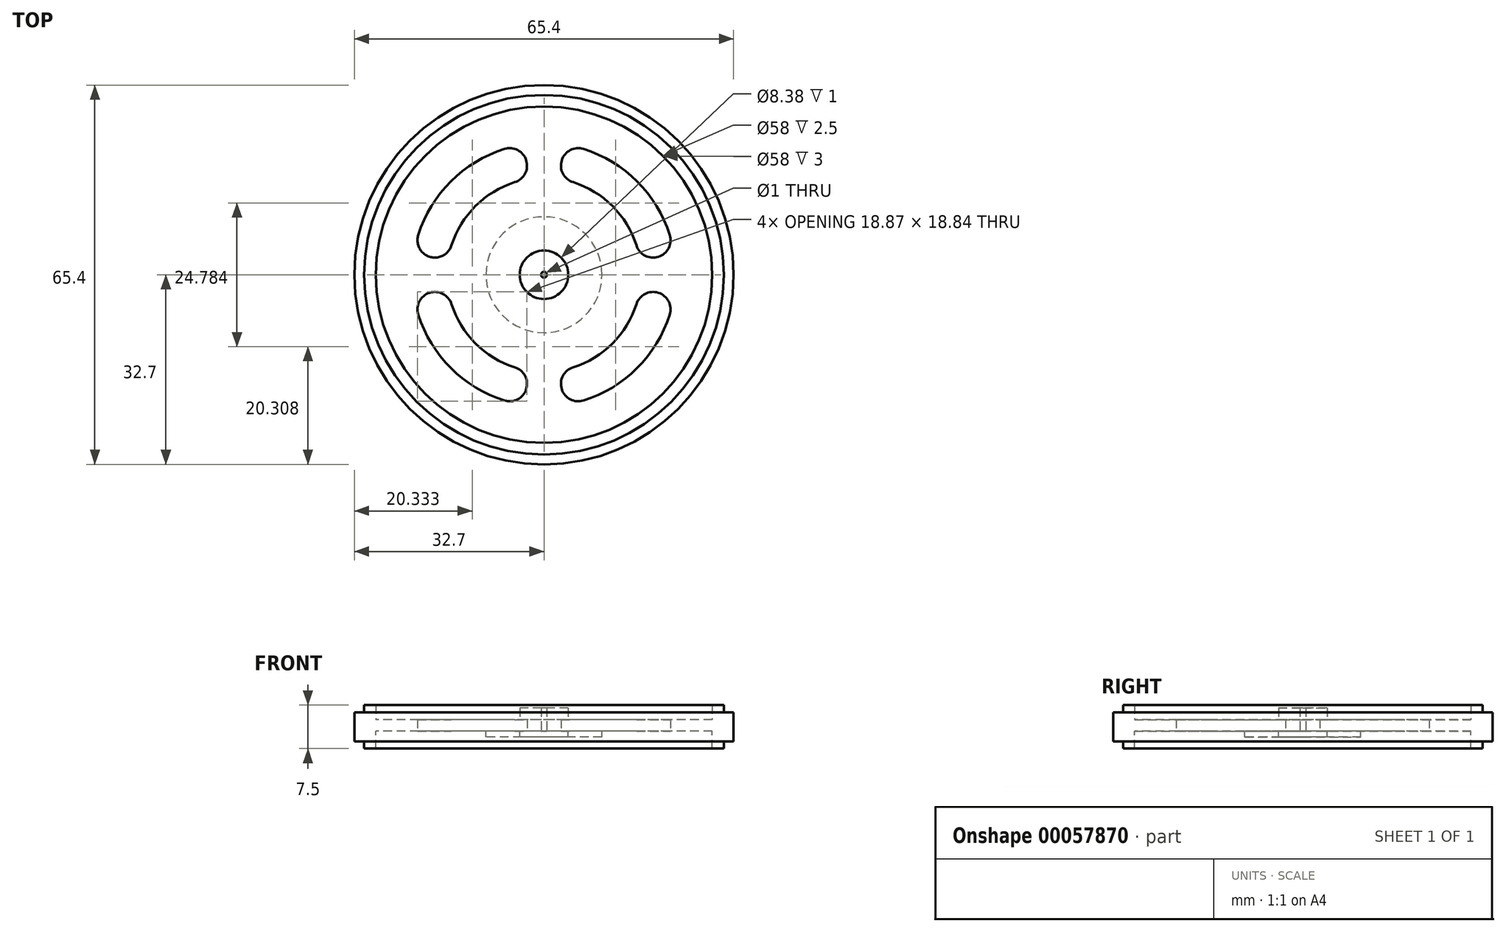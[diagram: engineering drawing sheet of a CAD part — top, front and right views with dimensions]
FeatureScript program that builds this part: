
annotation { "Feature Type Name" : "Feature", "Feature Type Description" : "" }
export const myFeature = defineFeature(function(context is Context, id is Id, definition is map)
    precondition{}
    {
        {
            var Q0;
            Q0=qCreatedBy(makeId("Top.planeOp"),FACE);
            var sketch = newSketch(context, id + "F0", { "sketchPlane" : qUnion([Q0])});
            skCircle(sketch, "E0", {"center": v(0, 0) * mm, "radius": 32.7 * mm});
            skSolve(sketch);
        }
        {
            var Q0;
            Q0=makeQuery(id+"F0.imprint","IMPRINT",FACE,{"disambiguationData":[TD([[makeQuery(id+"F0.imprint","IMPRINT",EDGE,{"derivedFrom":sQuery(id+"F0.wireOp",EDGE,"E0")}),1.0]])]});
            var sketch = newSketch(context, id + "F1", { "sketchPlane" : qUnion([Q0])});
            skArc(sketch, "E1", {"start": v(-5.02, 15.96) * mm, "mid": v(-11.82, 11.84) * mm, "end": v(-15.95, 5.05) * mm});
            skArc(sketch, "E2", {"start": v(-6.82, 21.69) * mm, "mid": v(-16.06, 16.1) * mm, "end": v(-21.67, 6.87) * mm});
            skArc(sketch, "E3", {"start": v(-5.02, 15.96) * mm, "mid": v(-3.06, 19.72) * mm, "end": v(-6.82, 21.69) * mm});
            skArc(sketch, "E4", {"start": v(-21.67, 6.87) * mm, "mid": v(-19.72, 3.1) * mm, "end": v(-15.95, 5.05) * mm});
            skArc(sketch, "E5.MirrorCS", {"start": v(21.67, 6.87) * mm, "mid": v(19.72, 3.1) * mm, "end": v(15.95, 5.05) * mm});
            skArc(sketch, "E6.MirrorCS", {"start": v(5.02, 15.96) * mm, "mid": v(11.82, 11.84) * mm, "end": v(15.95, 5.05) * mm});
            skArc(sketch, "E7.MirrorCS", {"start": v(5.02, 15.96) * mm, "mid": v(3.06, 19.72) * mm, "end": v(6.82, 21.69) * mm});
            skArc(sketch, "E8.MirrorCS", {"start": v(6.82, 21.69) * mm, "mid": v(16.06, 16.1) * mm, "end": v(21.67, 6.87) * mm});
            skArc(sketch, "E9.MirrorCS", {"start": v(6.82, -21.69) * mm, "mid": v(16.06, -16.1) * mm, "end": v(21.67, -6.87) * mm});
            skArc(sketch, "E10.MirrorCS", {"start": v(-6.82, -21.69) * mm, "mid": v(-16.06, -16.1) * mm, "end": v(-21.67, -6.87) * mm});
            skArc(sketch, "E11.MirrorCS", {"start": v(5.02, -15.96) * mm, "mid": v(11.82, -11.84) * mm, "end": v(15.95, -5.05) * mm});
            skArc(sketch, "E12.MirrorCS", {"start": v(5.02, -15.96) * mm, "mid": v(3.06, -19.72) * mm, "end": v(6.82, -21.69) * mm});
            skArc(sketch, "E13.MirrorCS", {"start": v(-5.02, -15.96) * mm, "mid": v(-3.06, -19.72) * mm, "end": v(-6.82, -21.69) * mm});
            skArc(sketch, "E14.MirrorCS", {"start": v(-21.67, -6.87) * mm, "mid": v(-19.72, -3.1) * mm, "end": v(-15.95, -5.05) * mm});
            skArc(sketch, "E15.MirrorCS", {"start": v(21.67, -6.87) * mm, "mid": v(19.72, -3.1) * mm, "end": v(15.95, -5.05) * mm});
            skArc(sketch, "E16.MirrorCS", {"start": v(-5.02, -15.96) * mm, "mid": v(-11.82, -11.84) * mm, "end": v(-15.95, -5.05) * mm});
            skSolve(sketch);
        }
        {
            var Q0;
            Q0=qCreatedBy(makeId("Top.planeOp"),FACE);
            var sketch = newSketch(context, id + "F2", { "sketchPlane" : qUnion([Q0])});
            skCircle(sketch, "E17", {"center": v(0, 0) * mm, "radius": 10 * mm});
            skCircle(sketch, "E18", {"center": v(0, 0) * mm, "radius": 29 * mm});
            skCircle(sketch, "E19", {"center": v(0, 0) * mm, "radius": 31 * mm});
            skCircle(sketch, "E20", {"center": v(0, 0) * mm, "radius": 4.19 * mm});
            skSolve(sketch);
        }
        {
            var Q0;
            Q0=makeQuery(id+"F1.imprint","IMPRINT",FACE,{"disambiguationData":[TD([[makeQuery(id+"F1.imprint","IMPRINT",EDGE,{"derivedFrom":sQuery(id+"F1.wireOp",EDGE,"E4")}),-1.0]])]});
            extrude(context, id + "F3", {"entities" : qUnion([Q0]), "depth" : 2 * mm});
        }
        {
            var Q0;
            Q0=makeQuery(id+"F2.imprint","IMPRINT",FACE,{"disambiguationData":[TD([[makeQuery(id+"F2.imprint","IMPRINT",EDGE,{"derivedFrom":sQuery(id+"F2.wireOp",EDGE,"E17")}),1.0]])]});
            extrude(context, id + "F4", {"entities" : qUnion([Q0]), "operationType" : NewBodyOperationType.ADD, "oppositeDirection" : true, "depth" : 1 * mm});
        }
        {
            var Q0;
            Q0=makeQuery(id+"F2.imprint","IMPRINT",FACE,{"disambiguationData":[TD([[makeQuery(id+"F2.imprint","IMPRINT",EDGE,{"derivedFrom":sQuery(id+"F2.wireOp",EDGE,"E18")}),-1.0]])]});
            extrude(context, id + "F5", {"entities" : qUnion([Q0]), "operationType" : NewBodyOperationType.ADD, "depth" : 4.5 * mm});
        }
        {
            var Q0;
            Q0=makeQuery(id+"F5.opExtrude","CAP_FACE",FACE,{"disambiguationData":[OSD([sQuery(id+"F2.wireOp",EDGE,"E18"),sQuery(id+"F2.wireOp",EDGE,"E19")])],"isStart":false});
            extrude(context, id + "F6", {"entities" : qUnion([Q0]), "operationType" : NewBodyOperationType.ADD, "oppositeDirection" : true, "depth" : 7.5 * mm});
        }
        {
            var Q0;
            {var subQ0=sQuery(id+"F0.wireOp",EDGE,"E0");var subQ1=makeQuery(id+"F3.opExtrude","SWEPT_FACE",FACE,{"disambiguationData":[OSD([subQ0])]});var subQ2=sQuery(id+"F1.wireOp",EDGE,"E15.MirrorCS");var subQ3=sQuery(id+"F1.wireOp",EDGE,"E10.MirrorCS");var subQ4=sQuery(id+"F1.wireOp",EDGE,"E8.MirrorCS");var subQ5=sQuery(id+"F1.wireOp",EDGE,"E7.MirrorCS");var subQ6=sQuery(id+"F1.wireOp",EDGE,"E6.MirrorCS");var subQ7=sQuery(id+"F1.wireOp",EDGE,"E5.MirrorCS");var subQ8=sQuery(id+"F1.wireOp",EDGE,"E4");var subQ9=sQuery(id+"F1.wireOp",EDGE,"E14.MirrorCS");var subQ10=sQuery(id+"F1.wireOp",EDGE,"E3");var subQ11=sQuery(id+"F1.wireOp",EDGE,"E2");var subQ12=sQuery(id+"F1.wireOp",EDGE,"E1");var subQ13=sQuery(id+"F1.wireOp",EDGE,"E16.MirrorCS");var subQ14=sQuery(id+"F1.wireOp",EDGE,"E9.MirrorCS");var subQ15=sQuery(id+"F1.wireOp",EDGE,"E12.MirrorCS");var subQ16=sQuery(id+"F1.wireOp",EDGE,"E13.MirrorCS");var subQ17=sQuery(id+"F1.wireOp",EDGE,"E11.MirrorCS");Q0=makeQuery(id+"F6.boolean.opBoolean","SPLIT",FACE,{"disambiguationData":[TD([subQ1])],"derivedFrom":makeQuery(id+"F4.boolean.opBoolean","SPLIT",FACE,{"disambiguationData":[TD([makeQuery(id+"F3.opExtrude","SWEPT_FACE",FACE,{"disambiguationData":[OSD([subQ8])]})])],"derivedFrom":makeQuery(id+"F3.opExtrude","CAP_FACE",FACE,{"disambiguationData":[OSD([subQ0,subQ8,subQ10,subQ11,subQ12,subQ6,subQ5,subQ4,subQ7,subQ3,subQ2,subQ13,subQ14,subQ9,subQ15,subQ16,subQ17])],"isStart":true})})});}
            extrude(context, id + "F7", {"entities" : qUnion([Q0]), "operationType" : NewBodyOperationType.ADD, "depth" : 0.87 * mm});
        }
        {
            var Q0;
            {var subQ0=sQuery(id+"F0.wireOp",EDGE,"E0");Q0=makeQuery(id+"F5.boolean.opBoolean","SPLIT",FACE,{"disambiguationData":[TD([makeQuery(id+"F3.opExtrude","SWEPT_FACE",FACE,{"disambiguationData":[OSD([subQ0])]})])],"derivedFrom":makeQuery(id+"F3.opExtrude","CAP_FACE",FACE,{"disambiguationData":[OSD([subQ0,sQuery(id+"F1.wireOp",EDGE,"E4"),sQuery(id+"F1.wireOp",EDGE,"E3"),sQuery(id+"F1.wireOp",EDGE,"E2"),sQuery(id+"F1.wireOp",EDGE,"E1"),sQuery(id+"F1.wireOp",EDGE,"E6.MirrorCS"),sQuery(id+"F1.wireOp",EDGE,"E7.MirrorCS"),sQuery(id+"F1.wireOp",EDGE,"E8.MirrorCS"),sQuery(id+"F1.wireOp",EDGE,"E5.MirrorCS"),sQuery(id+"F1.wireOp",EDGE,"E10.MirrorCS"),sQuery(id+"F1.wireOp",EDGE,"E15.MirrorCS"),sQuery(id+"F1.wireOp",EDGE,"E16.MirrorCS"),sQuery(id+"F1.wireOp",EDGE,"E9.MirrorCS"),sQuery(id+"F1.wireOp",EDGE,"E14.MirrorCS"),sQuery(id+"F1.wireOp",EDGE,"E12.MirrorCS"),sQuery(id+"F1.wireOp",EDGE,"E13.MirrorCS"),sQuery(id+"F1.wireOp",EDGE,"E11.MirrorCS")])],"isStart":false})});}
            extrude(context, id + "F8", {"entities" : qUnion([Q0]), "operationType" : NewBodyOperationType.ADD, "oppositeDirection" : true, "depth" : 3.75 * mm});
        }
        {
            var Q0;
            Q0=makeQuery(id+"F8.opExtrude","CAP_FACE",FACE,{"disambiguationData":[OSD([sQuery(id+"F0.wireOp",EDGE,"E0"),sQuery(id+"F1.wireOp",EDGE,"E4"),sQuery(id+"F1.wireOp",EDGE,"E3"),sQuery(id+"F1.wireOp",EDGE,"E2"),sQuery(id+"F1.wireOp",EDGE,"E1"),sQuery(id+"F1.wireOp",EDGE,"E6.MirrorCS"),sQuery(id+"F1.wireOp",EDGE,"E7.MirrorCS"),sQuery(id+"F1.wireOp",EDGE,"E8.MirrorCS"),sQuery(id+"F1.wireOp",EDGE,"E5.MirrorCS"),sQuery(id+"F1.wireOp",EDGE,"E10.MirrorCS"),sQuery(id+"F1.wireOp",EDGE,"E15.MirrorCS"),sQuery(id+"F1.wireOp",EDGE,"E16.MirrorCS"),sQuery(id+"F1.wireOp",EDGE,"E9.MirrorCS"),sQuery(id+"F1.wireOp",EDGE,"E14.MirrorCS"),sQuery(id+"F1.wireOp",EDGE,"E12.MirrorCS"),sQuery(id+"F1.wireOp",EDGE,"E13.MirrorCS"),sQuery(id+"F1.wireOp",EDGE,"E11.MirrorCS")])],"isStart":false});
            extrude(context, id + "F9", {"entities" : qUnion([Q0]), "operationType" : NewBodyOperationType.ADD, "oppositeDirection" : true, "depth" : 5 * mm});
        }
        {
            var Q0;
            Q0=sQuery(id+"F2.wireOp",VERTEX,"E20.center");
            var Q1;
            Q1=makeQuery(id+"F3.opExtrude","SWEPT_BODY",BODY,{"disambiguationData":[OSD([sQuery(id+"F0.wireOp",EDGE,"E0"),sQuery(id+"F1.wireOp",EDGE,"E4"),sQuery(id+"F1.wireOp",EDGE,"E3"),sQuery(id+"F1.wireOp",EDGE,"E2"),sQuery(id+"F1.wireOp",EDGE,"E1"),sQuery(id+"F1.wireOp",EDGE,"E6.MirrorCS"),sQuery(id+"F1.wireOp",EDGE,"E7.MirrorCS"),sQuery(id+"F1.wireOp",EDGE,"E8.MirrorCS"),sQuery(id+"F1.wireOp",EDGE,"E5.MirrorCS"),sQuery(id+"F1.wireOp",EDGE,"E10.MirrorCS"),sQuery(id+"F1.wireOp",EDGE,"E15.MirrorCS"),sQuery(id+"F1.wireOp",EDGE,"E16.MirrorCS"),sQuery(id+"F1.wireOp",EDGE,"E9.MirrorCS"),sQuery(id+"F1.wireOp",EDGE,"E14.MirrorCS"),sQuery(id+"F1.wireOp",EDGE,"E12.MirrorCS"),sQuery(id+"F1.wireOp",EDGE,"E13.MirrorCS"),sQuery(id+"F1.wireOp",EDGE,"E11.MirrorCS")])]});
            hole(context, id + "F10", {"style" : HoleStyle.SIMPLE, "holeDiameter" : 1 * mm, "endStyle" : HoleEndStyle.THROUGH, "oppositeDirection" : true, "locations" : qUnion([Q0]), "scope" : qUnion([Q1])});
        }
        {
            var Q0;
            Q0=makeQuery(id+"F2.imprint","IMPRINT",FACE,{"disambiguationData":[TD([[makeQuery(id+"F2.imprint","IMPRINT",EDGE,{"derivedFrom":sQuery(id+"F2.wireOp",EDGE,"E20")}),1.0]])]});
            extrude(context, id + "F11", {"entities" : qUnion([Q0]), "operationType" : NewBodyOperationType.ADD, "depth" : 4 * mm});
        }
        {
            var Q0;
            Q0=sQuery(id+"F2.wireOp",VERTEX,"E20.center");
            var Q1;
            Q1=makeQuery(id+"F3.opExtrude","SWEPT_BODY",BODY,{"disambiguationData":[OSD([sQuery(id+"F0.wireOp",EDGE,"E0"),sQuery(id+"F1.wireOp",EDGE,"E4"),sQuery(id+"F1.wireOp",EDGE,"E3"),sQuery(id+"F1.wireOp",EDGE,"E2"),sQuery(id+"F1.wireOp",EDGE,"E1"),sQuery(id+"F1.wireOp",EDGE,"E6.MirrorCS"),sQuery(id+"F1.wireOp",EDGE,"E7.MirrorCS"),sQuery(id+"F1.wireOp",EDGE,"E8.MirrorCS"),sQuery(id+"F1.wireOp",EDGE,"E5.MirrorCS"),sQuery(id+"F1.wireOp",EDGE,"E10.MirrorCS"),sQuery(id+"F1.wireOp",EDGE,"E15.MirrorCS"),sQuery(id+"F1.wireOp",EDGE,"E16.MirrorCS"),sQuery(id+"F1.wireOp",EDGE,"E9.MirrorCS"),sQuery(id+"F1.wireOp",EDGE,"E14.MirrorCS"),sQuery(id+"F1.wireOp",EDGE,"E12.MirrorCS"),sQuery(id+"F1.wireOp",EDGE,"E13.MirrorCS"),sQuery(id+"F1.wireOp",EDGE,"E11.MirrorCS")])]});
            hole(context, id + "F12", {"style" : HoleStyle.SIMPLE, "holeDiameter" : 1 * mm, "endStyle" : HoleEndStyle.THROUGH, "oppositeDirection" : true, "locations" : qUnion([Q0]), "scope" : qUnion([Q1])});
        }
    });
